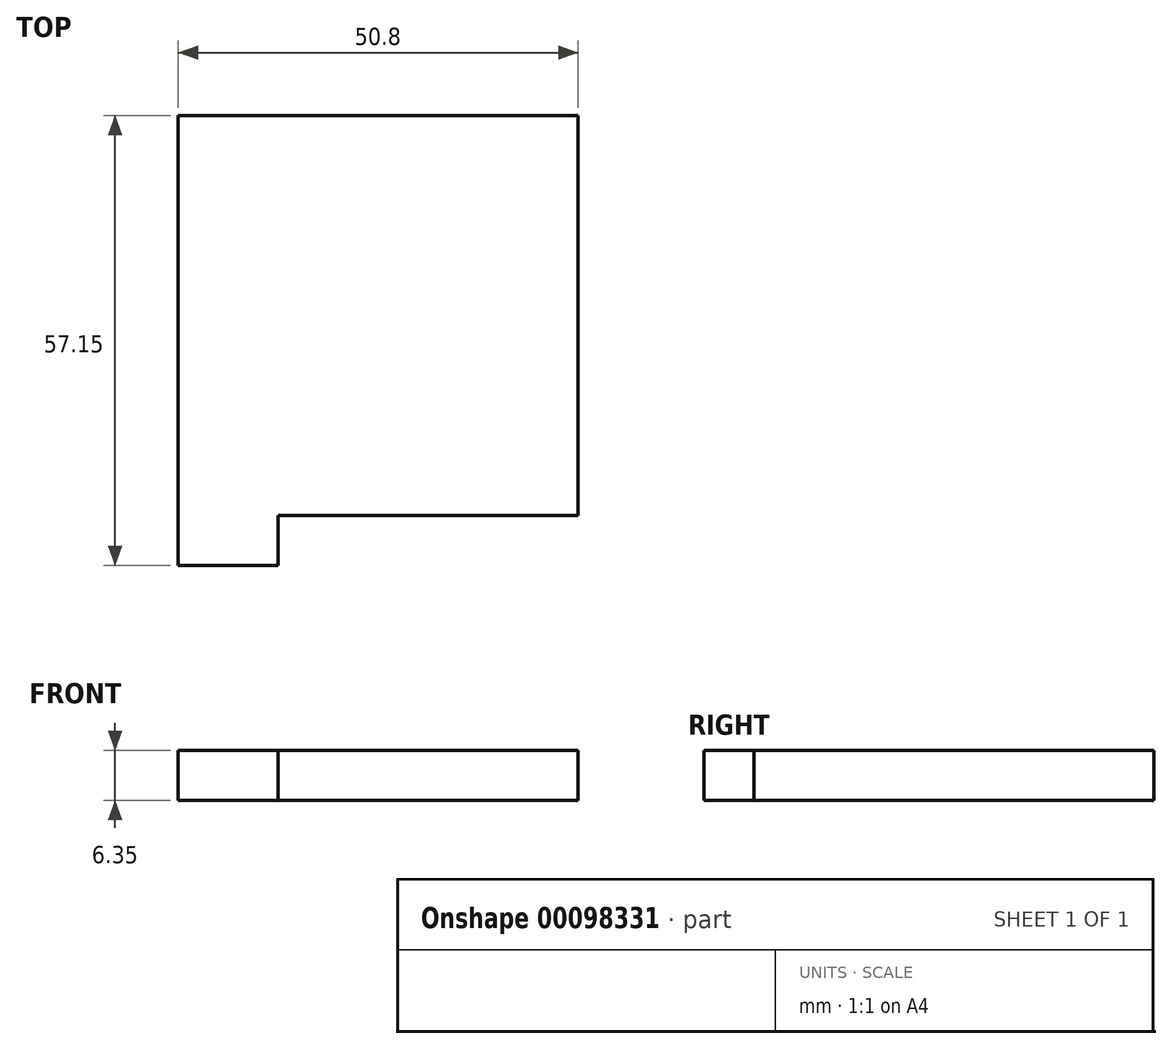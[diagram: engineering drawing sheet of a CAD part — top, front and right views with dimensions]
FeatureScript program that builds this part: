
annotation { "Feature Type Name" : "Feature", "Feature Type Description" : "" }
export const myFeature = defineFeature(function(context is Context, id is Id, definition is map)
    precondition{}
    {
        {
            var Q0;
            Q0=qCreatedBy(makeId("Top.planeOp"),FACE);
            var sketch = newSketch(context, id + "F0", { "sketchPlane" : qUnion([Q0])});
            skLineSegment(sketch, "E0.bottom", {"start": v(0, 0) * mm, "end": v(50.8, 0) * mm});
            skLineSegment(sketch, "E0.top", {"start": v(0, -50.8) * mm, "end": v(50.8, -50.8) * mm});
            skLineSegment(sketch, "E0.left", {"start": v(0, 0) * mm, "end": v(0, -50.8) * mm});
            skLineSegment(sketch, "E0.right", {"start": v(50.8, 0) * mm, "end": v(50.8, -50.8) * mm});
            skLineSegment(sketch, "E1.bottom", {"start": v(0, 0) * mm, "end": v(12.7, 0) * mm});
            skLineSegment(sketch, "E1.top", {"start": v(0, 6.35) * mm, "end": v(12.7, 6.35) * mm});
            skLineSegment(sketch, "E1.left", {"start": v(0, 0) * mm, "end": v(0, 6.35) * mm});
            skLineSegment(sketch, "E1.right", {"start": v(12.7, 0) * mm, "end": v(12.7, 6.35) * mm});
            skLineSegment(sketch, "E2.bottom", {"start": v(50.8, 0) * mm, "end": v(38.1, 0) * mm});
            skLineSegment(sketch, "E2.top", {"start": v(50.8, 6.35) * mm, "end": v(38.1, 6.35) * mm});
            skLineSegment(sketch, "E2.left", {"start": v(50.8, 0) * mm, "end": v(50.8, 6.35) * mm});
            skLineSegment(sketch, "E2.right", {"start": v(38.1, 0) * mm, "end": v(38.1, 6.35) * mm});
            skLineSegment(sketch, "E3.top", {"start": v(0, -57.15) * mm, "end": v(12.7, -57.15) * mm});
            skLineSegment(sketch, "E3.left", {"start": v(0, -50.8) * mm, "end": v(0, -57.15) * mm});
            skLineSegment(sketch, "E3.right", {"start": v(12.7, -50.8) * mm, "end": v(12.7, -57.15) * mm});
            skLineSegment(sketch, "E4.bottom", {"start": v(50.8, -50.8) * mm, "end": v(38.1, -50.8) * mm});
            skLineSegment(sketch, "E4.top", {"start": v(50.8, -57.15) * mm, "end": v(38.1, -57.15) * mm});
            skLineSegment(sketch, "E4.left", {"start": v(50.8, -50.8) * mm, "end": v(50.8, -57.15) * mm});
            skLineSegment(sketch, "E4.right", {"start": v(38.1, -50.8) * mm, "end": v(38.1, -57.15) * mm});
            skSolve(sketch);
        }
        {
            var Q0;
            Q0=makeQuery(id+"F0.imprint","IMPRINT",FACE,{"disambiguationData":[TD([[makeQuery(id+"F0.imprint","IMPRINT",EDGE,{"derivedFrom":sQuery(id+"F0.wireOp",EDGE,"E0.bottom")}),-1.0]])]});
            var Q1;
            Q1=makeQuery(id+"F0.imprint","IMPRINT",FACE,{"disambiguationData":[TD([[makeQuery(id+"F0.imprint","IMPRINT",EDGE,{"derivedFrom":sQuery(id+"F0.wireOp",EDGE,"E3.top")}),1.0]])]});
            var Q2;
            Q2=makeQuery(id+"F0.imprint","IMPRINT",FACE,{"disambiguationData":[TD([[makeQuery(id+"F0.imprint","IMPRINT",EDGE,{"derivedFrom":sQuery(id+"F0.wireOp",EDGE,"E4.bottom")}),1.0]])]});
            var Q3;
            Q3=makeQuery(id+"F0.imprint","IMPRINT",FACE,{"disambiguationData":[TD([[makeQuery(id+"F0.imprint","IMPRINT",EDGE,{"derivedFrom":sQuery(id+"F0.wireOp",EDGE,"E1.bottom")}),1.0]])]});
            var Q4;
            Q4=makeQuery(id+"F0.imprint","IMPRINT",FACE,{"disambiguationData":[TD([[makeQuery(id+"F0.imprint","IMPRINT",EDGE,{"derivedFrom":sQuery(id+"F0.wireOp",EDGE,"E2.bottom")}),-1.0]])]});
            extrude(context, id + "F1", {"entities" : qUnion([Q0, Q1, Q2, Q3, Q4]), "depth" : 6.35 * mm});
        }
    });
